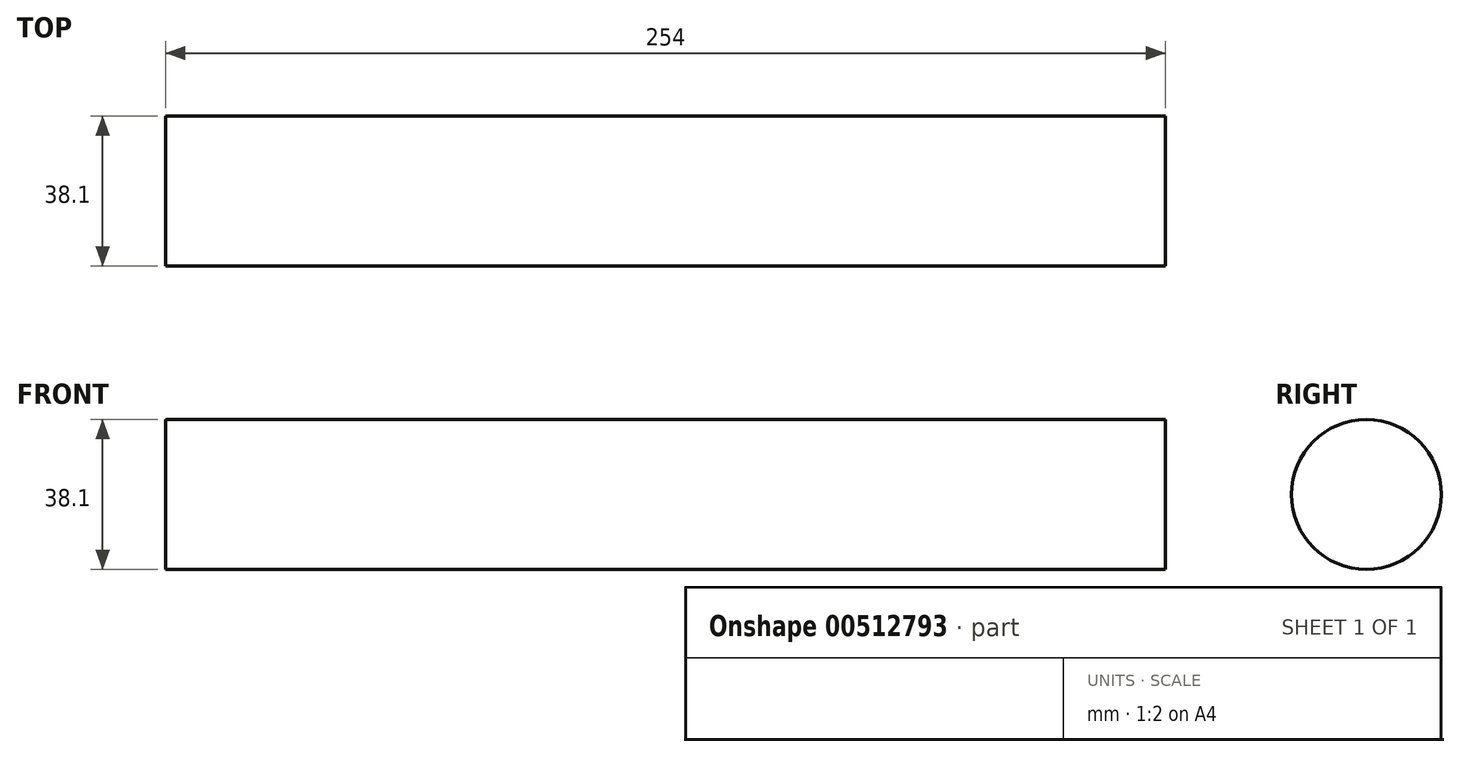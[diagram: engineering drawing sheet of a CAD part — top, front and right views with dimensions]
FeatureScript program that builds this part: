
annotation { "Feature Type Name" : "Feature", "Feature Type Description" : "" }
export const myFeature = defineFeature(function(context is Context, id is Id, definition is map)
    precondition{}
    {
        {
            var Q0;
            Q0=qCreatedBy(makeId("Right.planeOp"),FACE);
            var sketch = newSketch(context, id + "F0", { "sketchPlane" : qUnion([Q0])});
            skCircle(sketch, "E0", {"center": v(0, 0) * mm, "radius": 19.05 * mm});
            skSolve(sketch);
        }
        {
            var Q0;
            Q0=qSketchRegion(id+"F0",true);
            extrude(context, id + "F1", {"entities" : qUnion([Q0]), "depth" : 254 * mm});
        }
    });
